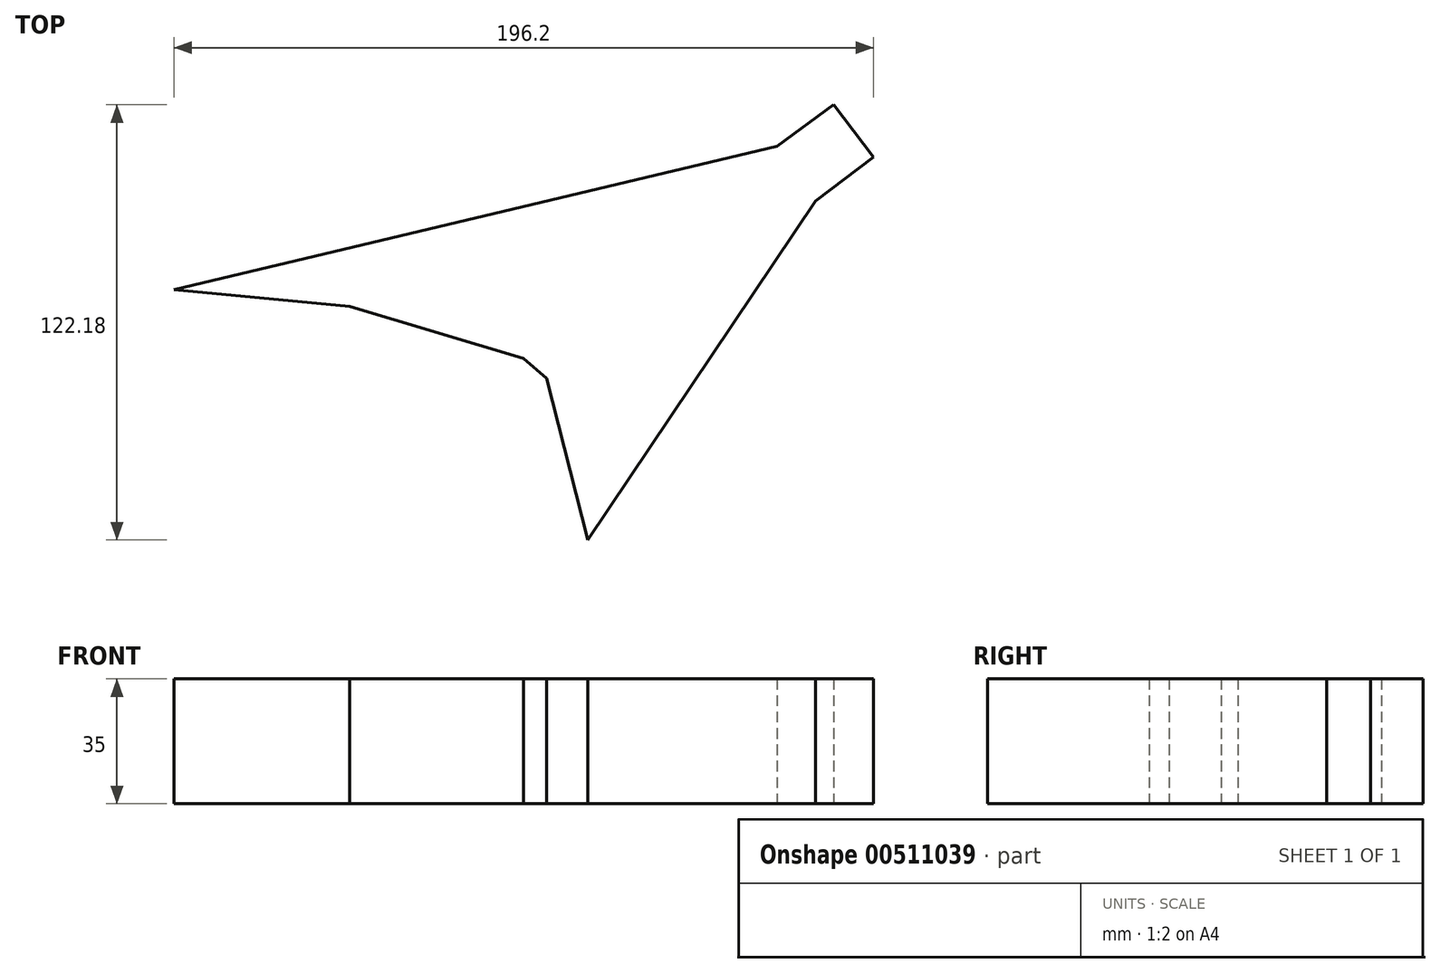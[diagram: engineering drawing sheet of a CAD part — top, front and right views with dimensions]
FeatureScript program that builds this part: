
annotation { "Feature Type Name" : "Feature", "Feature Type Description" : "" }
export const myFeature = defineFeature(function(context is Context, id is Id, definition is map)
    precondition{}
    {
        {
            var Q0;
            Q0=qCreatedBy(makeId("Top.planeOp"),FACE);
            var sketch = newSketch(context, id + "F0", { "sketchPlane" : qUnion([Q0])});
            skLineSegment(sketch, "E0.bottom", {"start": v(0, 0) * mm, "end": v(300, 0) * mm});
            skLineSegment(sketch, "E0.top", {"start": v(0, 200) * mm, "end": v(300, 200) * mm});
            skLineSegment(sketch, "E0.left", {"start": v(0, 0) * mm, "end": v(0, 200) * mm});
            skLineSegment(sketch, "E0.right", {"start": v(300, 0) * mm, "end": v(300, 200) * mm});
            skLineSegment(sketch, "E1", {"start": v(172.55, 118.84) * mm, "end": v(3.34, 78.58) * mm});
            skLineSegment(sketch, "E2", {"start": v(3.34, 78.58) * mm, "end": v(52.6, 73.86) * mm});
            skLineSegment(sketch, "E3", {"start": v(52.6, 73.86) * mm, "end": v(101.44, 59.3) * mm});
            skLineSegment(sketch, "E4", {"start": v(101.44, 59.3) * mm, "end": v(107.86, 53.73) * mm});
            skLineSegment(sketch, "E5", {"start": v(107.86, 53.73) * mm, "end": v(119.43, 8.32) * mm});
            skLineSegment(sketch, "E6", {"start": v(119.43, 8.32) * mm, "end": v(183.26, 103.42) * mm});
            skLineSegment(sketch, "E7", {"start": v(183.26, 103.42) * mm, "end": v(199.54, 115.84) * mm});
            skLineSegment(sketch, "E8", {"start": v(199.54, 115.84) * mm, "end": v(188.35, 130.5) * mm});
            skLineSegment(sketch, "E9", {"start": v(188.35, 130.5) * mm, "end": v(172.55, 118.84) * mm});
            skSolve(sketch);
        }
        {
            var Q0;
            Q0=makeQuery(id+"F0.imprint","IMPRINT",FACE,{"disambiguationData":[TD([[makeQuery(id+"F0.imprint","IMPRINT",EDGE,{"derivedFrom":sQuery(id+"F0.wireOp",EDGE,"E1")}),1.0]])]});
            extrude(context, id + "F1", {"entities" : qUnion([Q0]), "depth" : 35 * mm});
        }
    });
